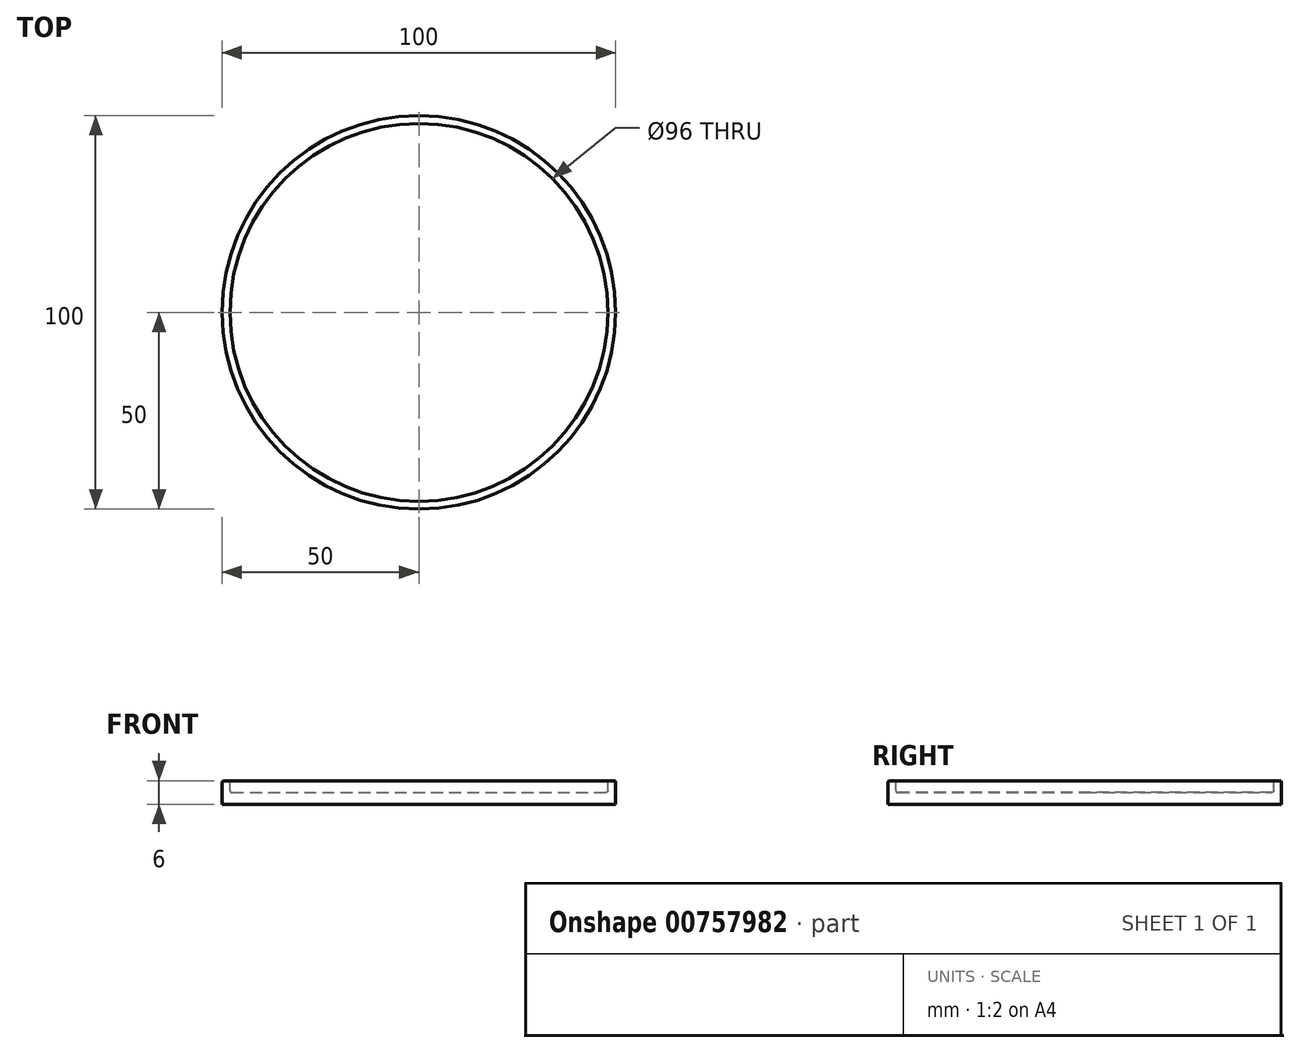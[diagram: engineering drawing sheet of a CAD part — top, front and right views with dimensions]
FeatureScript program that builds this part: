
annotation { "Feature Type Name" : "Feature", "Feature Type Description" : "" }
export const myFeature = defineFeature(function(context is Context, id is Id, definition is map)
    precondition{}
    {
        {
            var Q0;
            Q0=qCreatedBy(makeId("Front.planeOp"),FACE);
            var sketch = newSketch(context, id + "F0", { "sketchPlane" : qUnion([Q0])});
            skLineSegment(sketch, "E0", {"start": v(0, 0) * mm, "end": v(-50, 0) * mm});
            skLineSegment(sketch, "E1", {"start": v(-50, 0) * mm, "end": v(-50, 6) * mm});
            skLineSegment(sketch, "E2", {"start": v(-50, 6) * mm, "end": v(-48, 6) * mm});
            skLineSegment(sketch, "E3", {"start": v(-48, 6) * mm, "end": v(-48, 3) * mm});
            skLineSegment(sketch, "E4", {"start": v(-48, 3) * mm, "end": v(0, 3) * mm});
            skLineSegment(sketch, "E5", {"start": v(0, 3) * mm, "end": v(0, 0) * mm});
            skSolve(sketch);
        }
        {
            var Q0;
            Q0 = qSketchRegion(id + "F0", true);
            var Q1;
            Q1=sQuery(id+"F0.wireOp",EDGE,"E5");
            revolve(context, id + "F1", {"surfaceOperationType" : NewSurfaceOperationType.NEW, "entities" : qUnion([Q0]), "axis" : qUnion([Q1]), "revolveType" : RevolveType.FULL});
        }
        {
            var Q0;
            Q0=makeQuery(id+"F1.opRevolve","SWEPT_EDGE",EDGE,{"disambiguationData":[OSD([sQuery(id+"F0.wireOp",EDGE,"E1"),sQuery(id+"F0.wireOp",EDGE,"E2")])]});
            fillet(context, id + "F2", {"entities" : qUnion([Q0]), "radius" : .5 * mm, "tangentPropagation" : true, "allowEdgeOverflow" : false});
        }
        {
            var Q0;
            Q0=makeQuery(id+"F1.opRevolve","SWEPT_EDGE",EDGE,{"disambiguationData":[OSD([sQuery(id+"F0.wireOp",EDGE,"E2"),sQuery(id+"F0.wireOp",EDGE,"E3")])]});
            fillet(context, id + "F3", {"entities" : qUnion([Q0]), "radius" : .5 * mm, "tangentPropagation" : true, "allowEdgeOverflow" : false});
        }
        {
            var Q0;
            Q0=makeQuery(id+"F1.opRevolve","SWEPT_EDGE",EDGE,{"disambiguationData":[OSD([sQuery(id+"F0.wireOp",EDGE,"E3"),sQuery(id+"F0.wireOp",EDGE,"E4")])]});
            fillet(context, id + "F4", {"entities" : qUnion([Q0]), "radius" : .5 * mm, "tangentPropagation" : true, "allowEdgeOverflow" : false});
        }
    });
